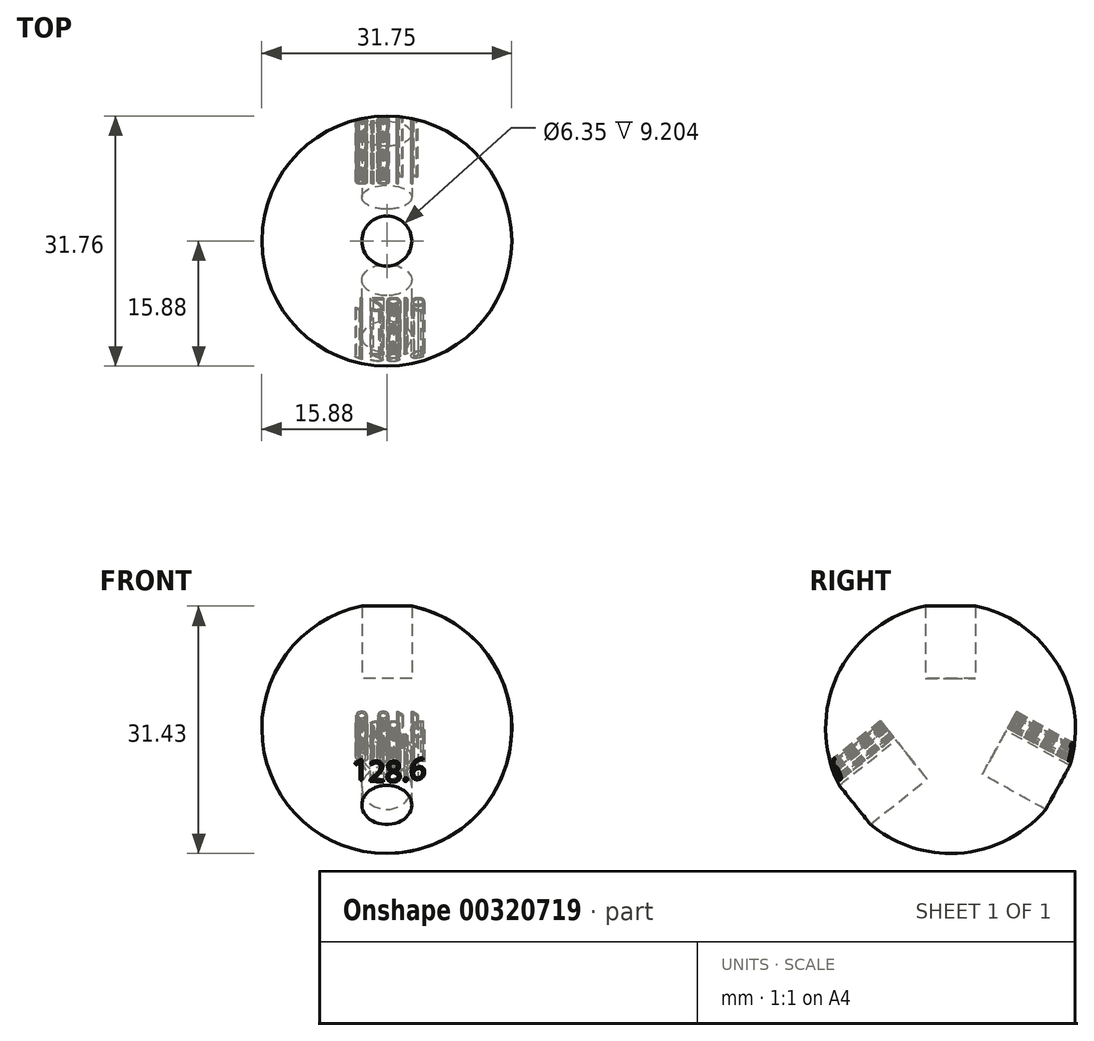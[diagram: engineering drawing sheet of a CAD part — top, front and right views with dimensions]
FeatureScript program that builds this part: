
annotation { "Feature Type Name" : "Feature", "Feature Type Description" : "" }
export const myFeature = defineFeature(function(context is Context, id is Id, definition is map)
    precondition{}
    {
        {
            var Q0;
            Q0=qCreatedBy(makeId("Front.planeOp"),FACE);
            var sketch = newSketch(context, id + "F0", { "sketchPlane" : qUnion([Q0])});
            skArc(sketch, "E0", {"start": v(0, 15.88) * mm, "mid": v(-15.88, 0) * mm, "end": v(0, -15.88) * mm});
            skLineSegment(sketch, "E1", {"start": v(0, 15.88) * mm, "end": v(0, -15.88) * mm});
            skSolve(sketch);
        }
        {
            var Q0;
            Q0=qCreatedBy(makeId("Top.planeOp"),FACE);
            var sketch = newSketch(context, id + "F1", { "sketchPlane" : qUnion([Q0])});
            skCircle(sketch, "E2", {"center": v(0, 0) * mm, "radius": 15.88 * mm});
            skSolve(sketch);
        }
        {
            var Q0;
            Q0=makeQuery(id+"F0.imprint","IMPRINT",FACE,{"disambiguationData":[TD([[makeQuery(id+"F0.imprint","IMPRINT",EDGE,{"derivedFrom":sQuery(id+"F0.wireOp",EDGE,"E0")}),1.0]])]});
            var Q1;
            Q1=sQuery(id+"F1.wireOp",EDGE,"E2");
            revolve(context, id + "F2", {"entities" : qUnion([Q0]), "axis" : qUnion([Q1]), "revolveType" : RevolveType.FULL});
        }
        {
            var Q0;
            Q0=qCreatedBy(makeId("Top.planeOp"),FACE);
            cPlane(context, id + "F3", {"entities" : qUnion([Q0]), "cplaneType" : CPlaneType.OFFSET, "offset" : 6.35 * mm, "width" : 152.4 * mm, "height" : 152.4 * mm});
        }
        {
            var Q0;
            Q0=qCreatedBy(id+"F3.planeOp",FACE);
            var sketch = newSketch(context, id + "F4", { "sketchPlane" : qUnion([Q0])});
            skCircle(sketch, "E3", {"center": v(0, 0) * mm, "radius": 3.18 * mm});
            skSolve(sketch);
        }
        {
            var Q0;
            Q0=qSketchRegion(id+"F4",true);
            extrude(context, id + "F5", {"entities" : qUnion([Q0]), "depth" : 50.8 * mm});
        }
        {
            var Q0;
            Q0=qCreatedBy(makeId("Front.planeOp"),FACE);
            var sketch = newSketch(context, id + "F6", { "sketchPlane" : qUnion([Q0])});
            skLineSegment(sketch, "E4", {"start": v(0, 0) * mm, "end": v(53.83, 0) * mm, "construction": true});
            skSolve(sketch);
        }
        {
            var Q0;
            Q0=makeQuery(id+"F5.opExtrude","SWEPT_BODY",BODY,{"disambiguationData":[OSD([sQuery(id+"F4.wireOp",EDGE,"E3")])]});
            var Q1;
            Q1=sQuery(id+"F6.wireOp",EDGE,"E4");
            transform(context, id + "F7", {"entities" : qUnion([Q0]), "transformType" : TransformType.ROTATION, "transformAxis" : qUnion([Q1]), "angle" : 128.6 * degree, "makeCopy" : true});
        }
        {
            var Q0;
            Q0=makeQuery(id+"F5.opExtrude","SWEPT_BODY",BODY,{"disambiguationData":[OSD([sQuery(id+"F4.wireOp",EDGE,"E3")])]});
            var Q1;
            Q1=sQuery(id+"F6.wireOp",EDGE,"E4");
            transform(context, id + "F8", {"entities" : qUnion([Q0]), "transformType" : TransformType.ROTATION, "transformAxis" : qUnion([Q1]), "angle" : 118.8 * degree, "oppositeDirection" : true, "makeCopy" : true});
        }
        {
            var Q0;
            Q0=makeQuery(id+"F7.opPattern","COPY",FACE,{"derivedFrom":makeQuery(id+"F5.opExtrude","CAP_FACE",FACE,{"disambiguationData":[OSD([sQuery(id+"F4.wireOp",EDGE,"E3")])],"isStart":false}),"instanceName":"1"});
            cPlane(context, id + "F9", {"entities" : qUnion([Q0]), "cplaneType" : CPlaneType.OFFSET, "offset" : 31.75 * mm, "oppositeDirection" : true, "width" : 152.4 * mm, "height" : 152.4 * mm});
        }
        {
            var Q0;
            Q0=qCreatedBy(id+"F9.planeOp",FACE);
            var sketch = newSketch(context, id + "F10", { "sketchPlane" : qUnion([Q0])});
            skText(sketch, "E5", { "text": "128.6\n", "fontName": "OpenSans-Regular.ttf"});
            const initialGuessF10  = {"E5": [-0.0044, 0.00365, 1, 0, 0.00265]};
            skSetInitialGuess(sketch, initialGuessF10);
            skSolve(sketch);
        }
        {
            var Q0;
            Q0=qSketchRegion(id+"F10",true);
            extrude(context, id + "F11", {"entities" : qUnion([Q0]), "operationType" : NewBodyOperationType.REMOVE, "oppositeDirection" : true, "depth" : 19.05 * mm});
        }
        {
            var Q0;
            Q0=makeQuery(id+"F8.opPattern","COPY",FACE,{"derivedFrom":makeQuery(id+"F5.opExtrude","CAP_FACE",FACE,{"disambiguationData":[OSD([sQuery(id+"F4.wireOp",EDGE,"E3")])],"isStart":false}),"instanceName":"1"});
            cPlane(context, id + "F12", {"entities" : qUnion([Q0]), "cplaneType" : CPlaneType.OFFSET, "offset" : 31.75 * mm, "oppositeDirection" : true, "width" : 152.4 * mm, "height" : 152.4 * mm});
        }
        {
            var Q0;
            Q0=qCreatedBy(id+"F12.planeOp",FACE);
            var sketch = newSketch(context, id + "F13", { "sketchPlane" : qUnion([Q0])});
            skText(sketch, "E6", { "text": "118.8", "fontName": "OpenSans-Regular.ttf"});
            const initialGuessF13  = {"E6": [-0.00424, 0.00357, 1, 0, 0.00236]};
            skSetInitialGuess(sketch, initialGuessF13);
            skSolve(sketch);
        }
        {
            var Q0;
            Q0=qSketchRegion(id+"F13",true);
            extrude(context, id + "F14", {"entities" : qUnion([Q0]), "operationType" : NewBodyOperationType.REMOVE, "oppositeDirection" : true, "depth" : 19.05 * mm});
        }
        {
            var Q0;
            Q0=makeQuery(id+"F5.opExtrude","SWEPT_BODY",BODY,{"disambiguationData":[OSD([sQuery(id+"F4.wireOp",EDGE,"E3")])]});
            var Q1;
            Q1=makeQuery(id+"F7.opPattern","COPY",BODY,{"derivedFrom":makeQuery(id+"F5.opExtrude","SWEPT_BODY",BODY,{"disambiguationData":[OSD([sQuery(id+"F4.wireOp",EDGE,"E3")])]}),"instanceName":"1"});
            var Q2;
            Q2=makeQuery(id+"F8.opPattern","COPY",BODY,{"derivedFrom":makeQuery(id+"F5.opExtrude","SWEPT_BODY",BODY,{"disambiguationData":[OSD([sQuery(id+"F4.wireOp",EDGE,"E3")])]}),"instanceName":"1"});
            var Q3;
            Q3=makeQuery(id+"F2.opRevolve","SWEPT_BODY",BODY,{"disambiguationData":[OSD([sQuery(id+"F0.wireOp",EDGE,"E0"),sQuery(id+"F0.wireOp",EDGE,"E1")])]});
            booleanBodies(context, id + "F15", {"operationType" : BooleanOperationType.SUBTRACTION, "tools" : qUnion([Q0, Q1, Q2]), "targets" : qUnion([Q3])});
        }
    });
